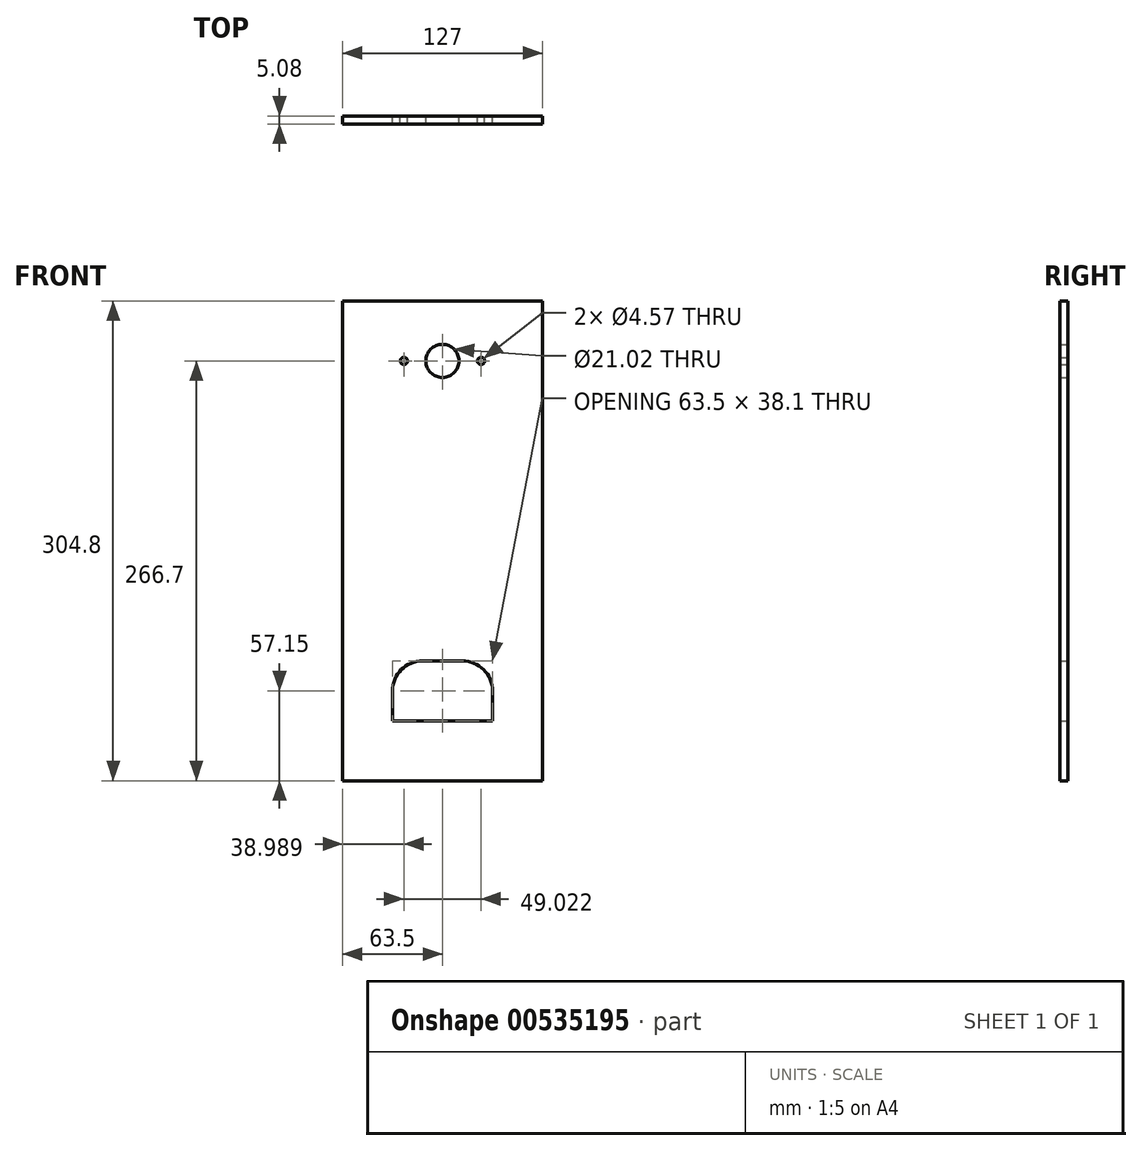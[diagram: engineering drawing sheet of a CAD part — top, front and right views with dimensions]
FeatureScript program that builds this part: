
annotation { "Feature Type Name" : "Feature", "Feature Type Description" : "" }
export const myFeature = defineFeature(function(context is Context, id is Id, definition is map)
    precondition{}
    {
        {
            var Q0;
            Q0=qCreatedBy(makeId("Front.planeOp"),FACE);
            var sketch = newSketch(context, id + "F0", { "sketchPlane" : qUnion([Q0])});
            skLineSegment(sketch, "E0.bottom", {"start": v(0, 0) * mm, "end": v(127, 0) * mm});
            skLineSegment(sketch, "E0.top", {"start": v(0, -304.8) * mm, "end": v(127, -304.8) * mm});
            skLineSegment(sketch, "E0.left", {"start": v(0, 0) * mm, "end": v(0, -304.8) * mm});
            skLineSegment(sketch, "E0.right", {"start": v(127, 0) * mm, "end": v(127, -304.8) * mm});
            skCircle(sketch, "E1", {"center": v(63.5, -38.1) * mm, "radius": 10.5 * mm});
            skLineSegment(sketch, "E2", {"start": v(63.5, 0) * mm, "end": v(63.5, -304.8) * mm, "construction": true});
            skCircle(sketch, "E3", {"center": v(88.01, -38.1) * mm, "radius": 2.29 * mm});
            skLineSegment(sketch, "E4", {"start": v(63.5, -38.1) * mm, "end": v(127, -38.1) * mm, "construction": true});
            skCircle(sketch, "E5.MirrorC", {"center": v(38.99, -38.1) * mm, "radius": 2.29 * mm});
            skLineSegment(sketch, "E6.bottom", {"start": v(31.75, -266.7) * mm, "end": v(95.25, -266.7) * mm});
            skLineSegment(sketch, "E6.top", {"start": v(50.8, -228.6) * mm, "end": v(76.2, -228.6) * mm});
            skLineSegment(sketch, "E6.left", {"start": v(31.75, -266.7) * mm, "end": v(31.75, -247.65) * mm});
            skLineSegment(sketch, "E6.right", {"start": v(95.25, -266.7) * mm, "end": v(95.25, -247.65) * mm});
            skPoint(sketch, "E7.visualSharp", {"position": v(31.75, -228.6) * mm});
            skArc(sketch, "E7.filletArc", {"start": v(50.8, -228.6) * mm, "mid": v(37.33, -234.18) * mm, "end": v(31.75, -247.65) * mm});
            skPoint(sketch, "E8.visualSharp", {"position": v(95.25, -228.6) * mm});
            skArc(sketch, "E8.filletArc", {"start": v(95.25, -247.65) * mm, "mid": v(89.67, -234.18) * mm, "end": v(76.2, -228.6) * mm});
            skSolve(sketch);
        }
        {
            var Q0;
            Q0=qSketchRegion(id+"F0",true);
            extrude(context, id + "F1", {"entities" : qUnion([Q0]), "depth" : 5.08 * mm});
        }
    });
